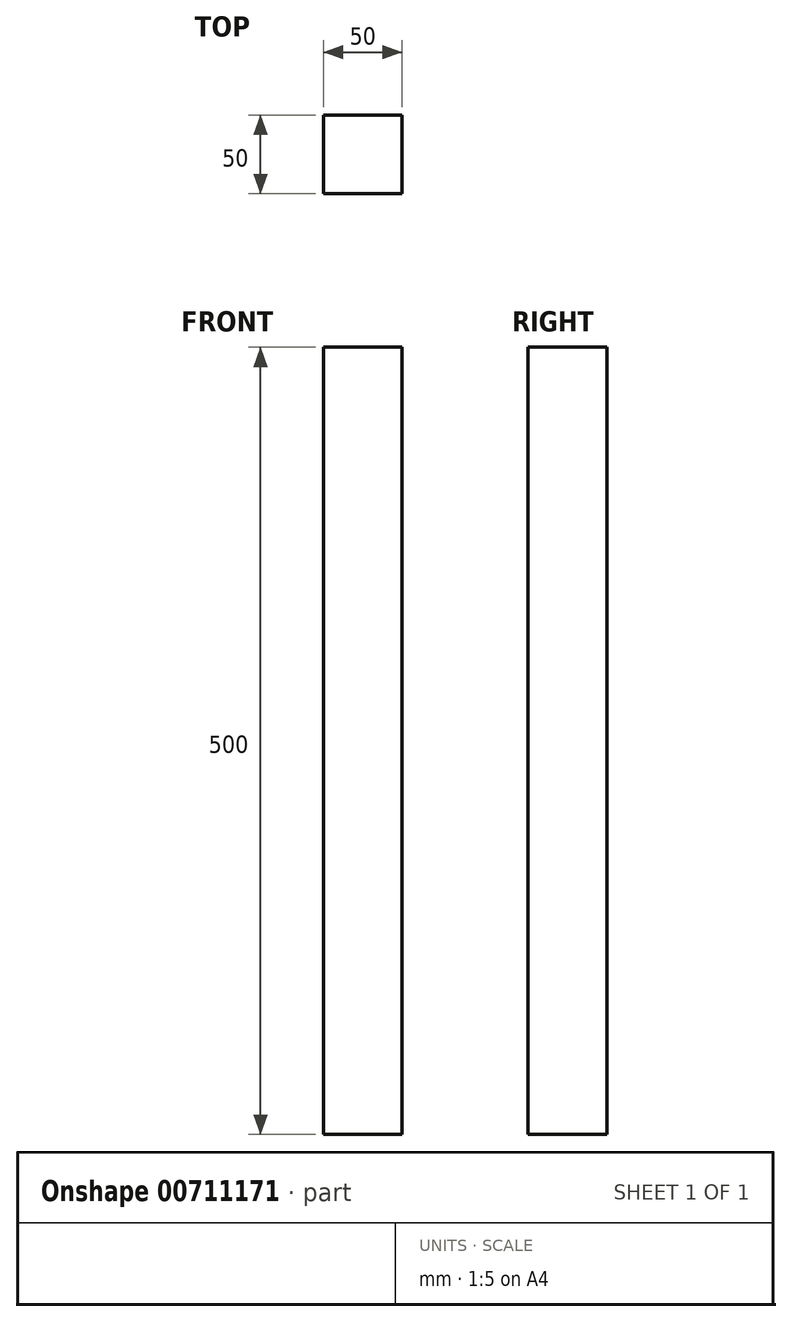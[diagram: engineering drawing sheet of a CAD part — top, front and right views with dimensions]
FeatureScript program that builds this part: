
annotation { "Feature Type Name" : "Feature", "Feature Type Description" : "" }
export const myFeature = defineFeature(function(context is Context, id is Id, definition is map)
    precondition{}
    {
        {
            var Q0;
            Q0=qCreatedBy(makeId("Top.planeOp"),FACE);
            var sketch = newSketch(context, id + "F0", { "sketchPlane" : qUnion([Q0])});
            skLineSegment(sketch, "E0.bottom", {"start": v(0, 0) * mm, "end": v(50, 0) * mm});
            skLineSegment(sketch, "E0.top", {"start": v(0, 50) * mm, "end": v(50, 50) * mm});
            skLineSegment(sketch, "E0.left", {"start": v(0, 0) * mm, "end": v(0, 50) * mm});
            skLineSegment(sketch, "E0.right", {"start": v(50, 0) * mm, "end": v(50, 50) * mm});
            skSolve(sketch);
        }
        {
            var Q0;
            Q0=makeQuery(id+"F0.imprint","IMPRINT",FACE,{"disambiguationData":[TD([[makeQuery(id+"F0.imprint","IMPRINT",EDGE,{"derivedFrom":sQuery(id+"F0.wireOp",EDGE,"E0.bottom")}),1.0]])]});
            extrude(context, id + "F1", {"entities" : qUnion([Q0]), "depth" : 500 * mm, "offsetDistance" : 25 * mm});
        }
    });
